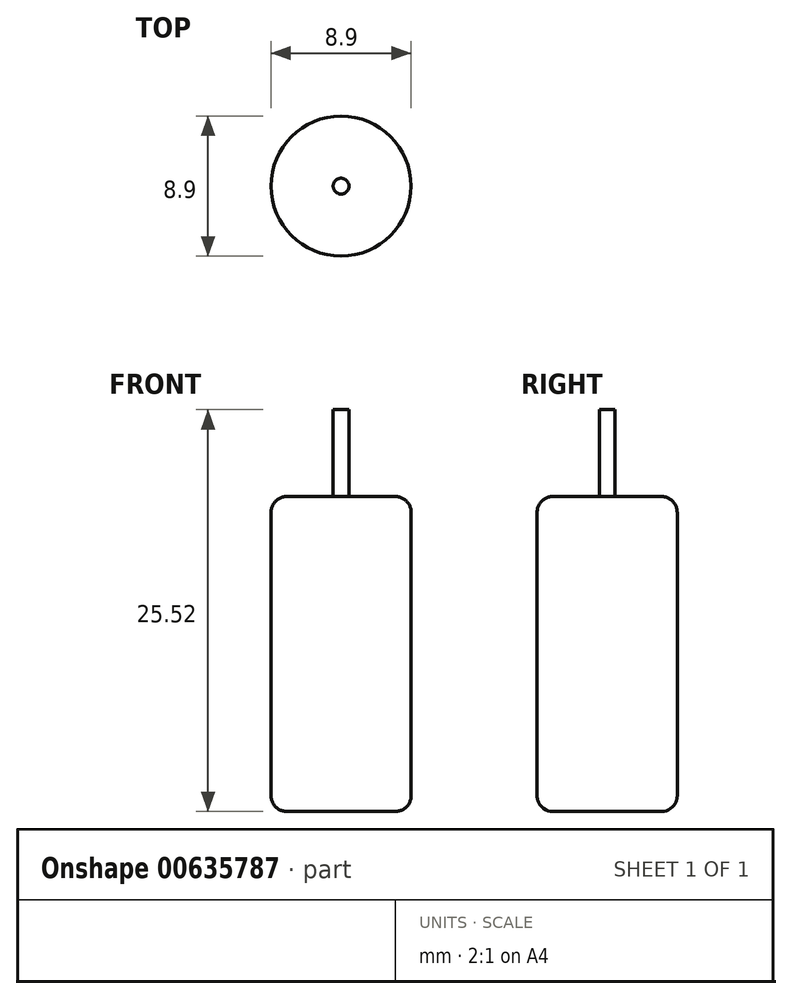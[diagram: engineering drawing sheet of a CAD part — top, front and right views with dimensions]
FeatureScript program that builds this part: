
annotation { "Feature Type Name" : "Feature", "Feature Type Description" : "" }
export const myFeature = defineFeature(function(context is Context, id is Id, definition is map)
    precondition{}
    {
        {
            var Q0;
            Q0=qCreatedBy(makeId("Top.planeOp"),FACE);
            var sketch = newSketch(context, id + "F0", { "sketchPlane" : qUnion([Q0])});
            skCircle(sketch, "E0", {"center": v(0, 0) * mm, "radius": 4.45 * mm});
            skSolve(sketch);
        }
        {
            var Q0;
            Q0 = qSketchRegion(id + "F0", true);
            extrude(context, id + "F1", {"entities" : qUnion([Q0]), "depth" : 20 * mm, "offsetDistance" : 25 * mm});
        }
        {
            var Q0;
            Q0=makeQuery(id+"F1.opExtrude","CAP_EDGE",EDGE,{"disambiguationData":[OSD([sQuery(id+"F0.wireOp",EDGE,"E0")])],"isStart":false});
            var Q1;
            Q1=makeQuery(id+"F1.opExtrude","CAP_EDGE",EDGE,{"disambiguationData":[OSD([sQuery(id+"F0.wireOp",EDGE,"E0")])],"isStart":true});
            fillet(context, id + "F2", {"entities" : qUnion([Q0, Q1]), "radius" : 1 * mm, "tangentPropagation" : true, "allowEdgeOverflow" : false});
        }
        {
            var Q0;
            Q0=makeQuery(id+"F1.opExtrude","CAP_FACE",FACE,{"disambiguationData":[OSD([sQuery(id+"F0.wireOp",EDGE,"E0")])],"isStart":false});
            var sketch = newSketch(context, id + "F3", { "sketchPlane" : qUnion([Q0])});
            skCircle(sketch, "E1", {"center": v(0, 0) * mm, "radius": 0.5 * mm});
            skSolve(sketch);
        }
        {
            var Q0;
            Q0 = qSketchRegion(id + "F3", true);
            extrude(context, id + "F4", {"entities" : qUnion([Q0]), "operationType" : NewBodyOperationType.ADD, "depth" : 5.52 * mm, "offsetDistance" : 25 * mm});
        }
    });
